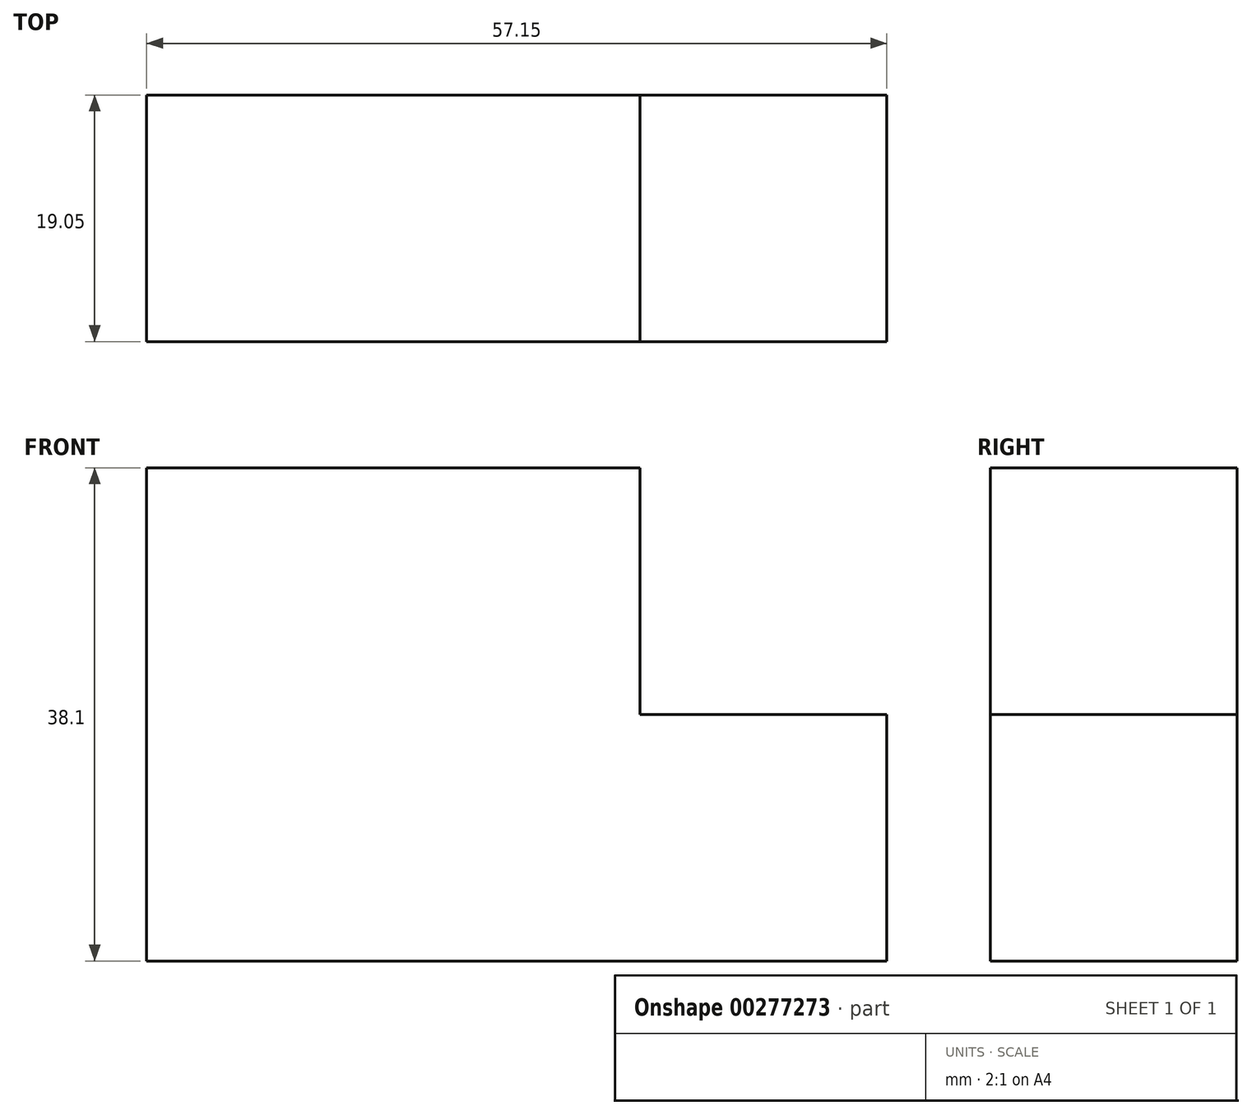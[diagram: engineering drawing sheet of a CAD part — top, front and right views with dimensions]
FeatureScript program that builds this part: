
annotation { "Feature Type Name" : "Feature", "Feature Type Description" : "" }
export const myFeature = defineFeature(function(context is Context, id is Id, definition is map)
    precondition{}
    {
        {
            var Q0;
            Q0=qCreatedBy(makeId("Front.planeOp"),FACE);
            var sketch = newSketch(context, id + "F0", { "sketchPlane" : qUnion([Q0])});
            skLineSegment(sketch, "E0.bottom", {"start": v(-31.16, 38.55) * mm, "end": v(-12.11, 38.55) * mm});
            skLineSegment(sketch, "E0.top", {"start": v(-31.16, 19.5) * mm, "end": v(-12.11, 19.5) * mm});
            skLineSegment(sketch, "E0.left", {"start": v(-31.16, 38.55) * mm, "end": v(-31.16, 19.5) * mm});
            skLineSegment(sketch, "E0.right", {"start": v(-12.11, 38.55) * mm, "end": v(-12.11, 19.5) * mm});
            skLineSegment(sketch, "E1.bottom", {"start": v(-12.11, 38.55) * mm, "end": v(6.94, 38.55) * mm});
            skLineSegment(sketch, "E1.top", {"start": v(-12.11, 19.5) * mm, "end": v(6.94, 19.5) * mm});
            skLineSegment(sketch, "E1.right", {"start": v(6.94, 38.55) * mm, "end": v(6.94, 19.5) * mm});
            skLineSegment(sketch, "E2.top", {"start": v(-31.16, 0.45) * mm, "end": v(-12.11, 0.45) * mm});
            skLineSegment(sketch, "E2.left", {"start": v(-31.16, 19.5) * mm, "end": v(-31.16, 0.45) * mm});
            skLineSegment(sketch, "E2.right", {"start": v(-12.11, 19.5) * mm, "end": v(-12.11, 0.45) * mm});
            skLineSegment(sketch, "E3.bottom", {"start": v(-12.11, 0.45) * mm, "end": v(6.94, 0.45) * mm});
            skLineSegment(sketch, "E3.left", {"start": v(-12.11, 0.45) * mm, "end": v(-12.11, 19.5) * mm});
            skLineSegment(sketch, "E3.right", {"start": v(6.94, 0.45) * mm, "end": v(6.94, 19.5) * mm});
            skLineSegment(sketch, "E4.bottom", {"start": v(6.94, 0.45) * mm, "end": v(25.99, 0.45) * mm});
            skLineSegment(sketch, "E4.top", {"start": v(6.94, 19.5) * mm, "end": v(25.99, 19.5) * mm});
            skLineSegment(sketch, "E4.right", {"start": v(25.99, 0.45) * mm, "end": v(25.99, 19.5) * mm});
            skSolve(sketch);
        }
        {
            var Q0;
            Q0=makeQuery(id+"F0.imprint","IMPRINT",FACE,{"disambiguationData":[TD([[makeQuery(id+"F0.imprint","IMPRINT",EDGE,{"derivedFrom":sQuery(id+"F0.wireOp",EDGE,"E0.bottom")}),-1.0]])]});
            var Q1;
            Q1=makeQuery(id+"F0.imprint","IMPRINT",FACE,{"disambiguationData":[TD([[makeQuery(id+"F0.imprint","IMPRINT",EDGE,{"derivedFrom":sQuery(id+"F0.wireOp",EDGE,"E1.bottom")}),-1.0]])]});
            var Q2;
            Q2=makeQuery(id+"F0.imprint","IMPRINT",FACE,{"disambiguationData":[TD([[makeQuery(id+"F0.imprint","IMPRINT",EDGE,{"derivedFrom":sQuery(id+"F0.wireOp",EDGE,"E0.top")}),-1.0]])]});
            var Q3;
            Q3=makeQuery(id+"F0.imprint","IMPRINT",FACE,{"disambiguationData":[TD([[makeQuery(id+"F0.imprint","IMPRINT",EDGE,{"derivedFrom":sQuery(id+"F0.wireOp",EDGE,"E3.bottom")}),1.0]])]});
            var Q4;
            Q4=makeQuery(id+"F0.imprint","IMPRINT",FACE,{"disambiguationData":[TD([[makeQuery(id+"F0.imprint","IMPRINT",EDGE,{"derivedFrom":sQuery(id+"F0.wireOp",EDGE,"E4.bottom")}),1.0]])]});
            extrude(context, id + "F1", {"entities" : qUnion([Q0, Q1, Q2, Q3, Q4]), "depth" : 19.05 * mm});
        }
    });
